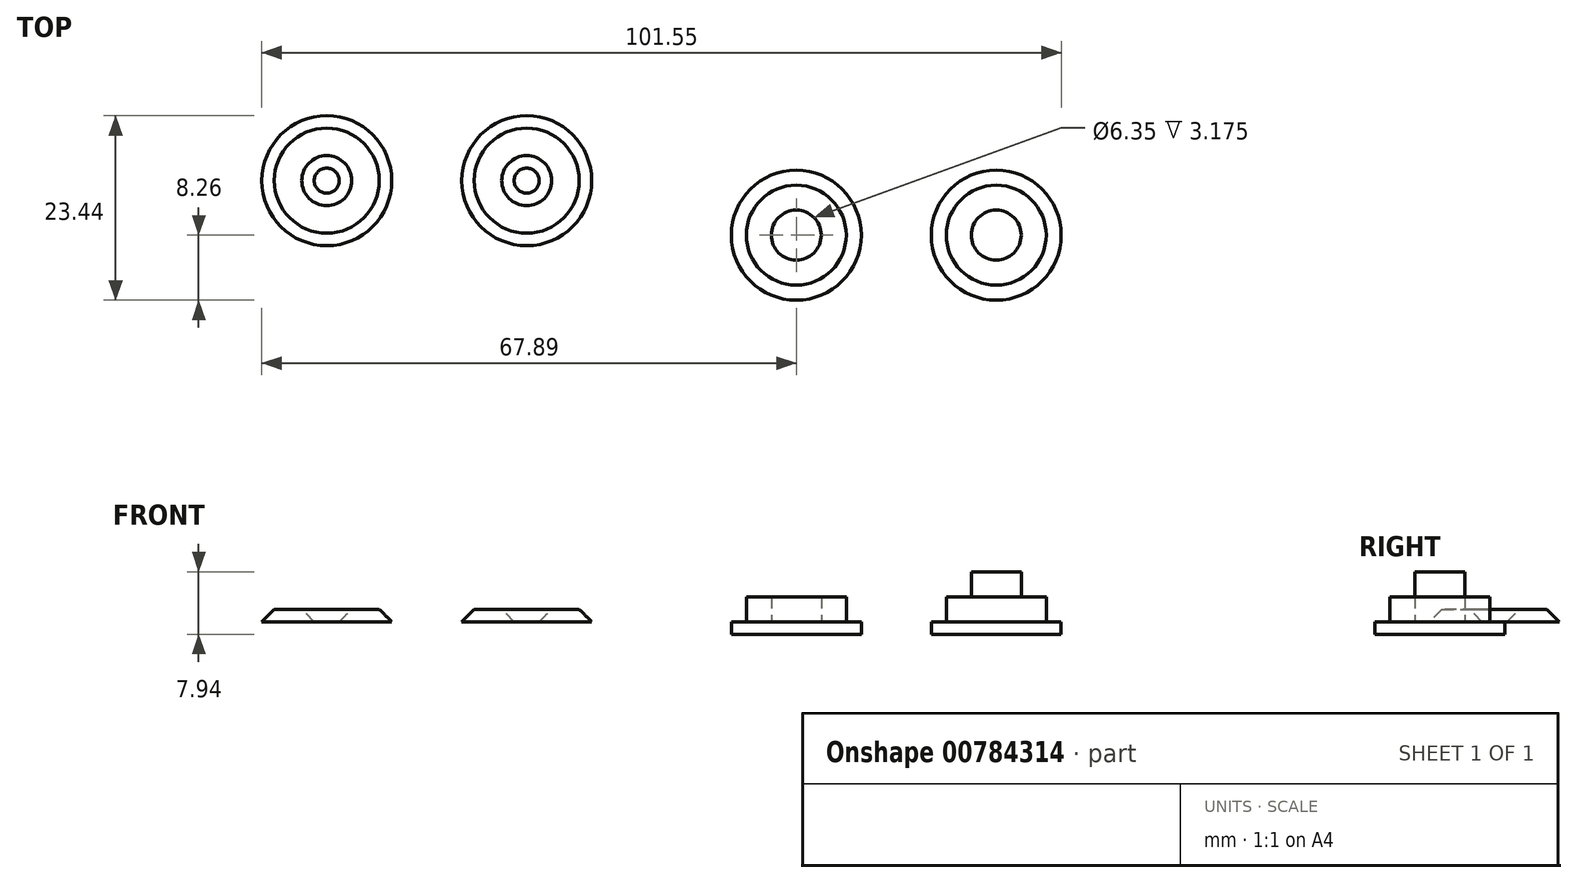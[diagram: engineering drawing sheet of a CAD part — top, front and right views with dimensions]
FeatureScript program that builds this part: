
annotation { "Feature Type Name" : "Feature", "Feature Type Description" : "" }
export const myFeature = defineFeature(function(context is Context, id is Id, definition is map)
    precondition{}
    {
        {
            var Q0;
            Q0=qCreatedBy(makeId("Top.planeOp"),FACE);
            var sketch = newSketch(context, id + "F0", { "sketchPlane" : qUnion([Q0])});
            skCircle(sketch, "E0", {"center": v(0, 0) * mm, "radius": 6.35 * mm});
            skCircle(sketch, "E1", {"center": v(0, 0) * mm, "radius": 3.18 * mm});
            skSolve(sketch);
        }
        {
            var Q0;
            Q0 = qSketchRegion(id + "F0", true);
            extrude(context, id + "F1", {"entities" : qUnion([Q0]), "depth" : 3.17 * mm, "offsetDistance" : 25.4 * mm});
        }
        {
            var Q0;
            Q0=makeQuery(id+"F1.opExtrude","CAP_FACE",FACE,{"disambiguationData":[OSD([sQuery(id+"F0.wireOp",EDGE,"E0"),sQuery(id+"F0.wireOp",EDGE,"E1")])],"isStart":true});
            var sketch = newSketch(context, id + "F2", { "sketchPlane" : qUnion([Q0])});
            skCircle(sketch, "E2", {"center": v(0, 0) * mm, "radius": 8.26 * mm});
            skSolve(sketch);
        }
        {
            var Q0;
            Q0 = qSketchRegion(id + "F2", true);
            extrude(context, id + "F3", {"entities" : qUnion([Q0]), "operationType" : NewBodyOperationType.ADD, "depth" : 3.17 * mm, "offsetDistance" : 25.4 * mm});
        }
        {
            var Q0;
            Q0=makeQuery(id+"F1.opExtrude","SWEPT_BODY",BODY,{"disambiguationData":[OSD([sQuery(id+"F0.wireOp",EDGE,"E0"),sQuery(id+"F0.wireOp",EDGE,"E1")])]});
            var Q1;
            Q1=qCreatedBy(makeId("Right.planeOp"),FACE);
            transform(context, id + "F4", {"entities" : qUnion([Q0]), "transformType" : TransformType.TRANSLATION_DISTANCE, "transformDirection" : qUnion([Q1]), "distance" : 25.4 * mm, "makeCopy" : true});
        }
        {
            var Q0;
            Q0=qCreatedBy(makeId("Top.planeOp"),FACE);
            var sketch = newSketch(context, id + "F5", { "sketchPlane" : qUnion([Q0])});
            skCircle(sketch, "E3", {"center": v(54.82, 6.15) * mm, "radius": 3.18 * mm});
            skSolve(sketch);
        }
        {
            var Q0;
            Q0 = qSketchRegion(id + "F5", true);
            extrude(context, id + "F6", {"entities" : qUnion([Q0]), "depth" : 6.35 * mm, "offsetDistance" : 25.4 * mm});
        }
        {
            var Q0;
            Q0=makeQuery(id+"F6.opExtrude","CAP_FACE",FACE,{"disambiguationData":[OSD([sQuery(id+"F5.wireOp",EDGE,"E3")])],"isStart":false});
            var sketch = newSketch(context, id + "F7", { "sketchPlane" : qUnion([Q0])});
            skLineSegment(sketch, "E4.bottom", {"start": v(54.82, 4.88) * mm, "end": v(58.63, 4.88) * mm});
            skLineSegment(sketch, "E4.top", {"start": v(54.82, 7.42) * mm, "end": v(58.63, 7.42) * mm});
            skLineSegment(sketch, "E4.left", {"start": v(54.82, 4.88) * mm, "end": v(54.82, 7.42) * mm});
            skLineSegment(sketch, "E4.right", {"start": v(58.63, 4.88) * mm, "end": v(58.63, 7.42) * mm});
            skLineSegment(sketch, "E5", {"start": v(54.82, 6.15) * mm, "end": v(54.82, 2.98) * mm});
            skLineSegment(sketch, "E6", {"start": v(54.82, 2.98) * mm, "end": v(54.82, 9.33) * mm});
            skSolve(sketch);
        }
        {
            var Q0;
            Q0 = qSketchRegion(id + "F7", true);
            extrude(context, id + "F8", {"entities" : qUnion([Q0]), "operationType" : NewBodyOperationType.ADD, "oppositeDirection" : true, "depth" : 3.17 * mm, "offsetDistance" : 25.4 * mm});
        }
        {
            var Q0;
            Q0=makeQuery(id+"F6.opExtrude","SWEPT_BODY",BODY,{"disambiguationData":[OSD([sQuery(id+"F5.wireOp",EDGE,"E3")])]});
            deleteBodies(context, id + "F9", {"entities" : qUnion([Q0])});
        }
        {
            var Q0;
            Q0=makeQuery(id+"F4.opPattern","COPY",FACE,{"derivedFrom":makeQuery(id+"F3.boolean.opBoolean","SPLIT",FACE,{"disambiguationData":[TD([makeQuery(id+"F1.opExtrude","SWEPT_FACE",FACE,{"disambiguationData":[OSD([sQuery(id+"F0.wireOp",EDGE,"E1")])]})])],"derivedFrom":makeQuery(id+"F3.opExtrude","CAP_FACE",FACE,{"disambiguationData":[OSD([sQuery(id+"F2.wireOp",EDGE,"E2")])],"isStart":true})}),"instanceName":"1"});
            extrude(context, id + "F10", {"entities" : qUnion([Q0]), "operationType" : NewBodyOperationType.ADD, "depth" : 6.35 * mm, "offsetDistance" : 25.4 * mm});
        }
        {
            var Q0;
            Q0=makeQuery(id+"F4.opPattern","COPY",FACE,{"derivedFrom":makeQuery(id+"F3.opExtrude","CAP_FACE",FACE,{"disambiguationData":[OSD([sQuery(id+"F2.wireOp",EDGE,"E2")])],"isStart":false}),"instanceName":"1"});
            extrude(context, id + "F11", {"entities" : qUnion([Q0]), "operationType" : NewBodyOperationType.REMOVE, "oppositeDirection" : true, "depth" : 1.59 * mm, "offsetDistance" : 25.4 * mm});
        }
        {
            var Q0;
            Q0=qCreatedBy(makeId("Top.planeOp"),FACE);
            var sketch = newSketch(context, id + "F12", { "sketchPlane" : qUnion([Q0])});
            skCircle(sketch, "E7", {"center": v(-34.24, 6.92) * mm, "radius": 8.26 * mm});
            skSolve(sketch);
        }
        {
            var Q0;
            Q0 = qSketchRegion(id + "F12", true);
            extrude(context, id + "F13", {"entities" : qUnion([Q0]), "depth" : 1.59 * mm, "offsetDistance" : 25.4 * mm, "hasDraft" : true, "draftAngle" : 45 * degree, "draftPullDirection" : true});
        }
        {
            var Q0;
            Q0=makeQuery(id+"F13.opExtrude","CAP_FACE",FACE,{"disambiguationData":[OSD([sQuery(id+"F12.wireOp",EDGE,"E7")])],"isStart":false});
            var sketch = newSketch(context, id + "F14", { "sketchPlane" : qUnion([Q0])});
            skCircle(sketch, "E8", {"center": v(-34.24, 6.92) * mm, "radius": 3.17 * mm});
            skSolve(sketch);
        }
        {
            var Q0;
            Q0=makeQuery(id+"F14.imprint","IMPRINT",FACE,{"disambiguationData":[TD([[makeQuery(id+"F14.imprint","IMPRINT",EDGE,{"derivedFrom":sQuery(id+"F14.wireOp",EDGE,"E8")}),1.0]])]});
            extrude(context, id + "F15", {"entities" : qUnion([Q0]), "operationType" : NewBodyOperationType.REMOVE, "oppositeDirection" : true, "depth" : 25.4 * mm, "offsetDistance" : 25.4 * mm, "hasDraft" : true, "draftAngle" : 45 * degree, "draftPullDirection" : true});
        }
        {
            var Q0;
            Q0=makeQuery(id+"F3.opExtrude","CAP_FACE",FACE,{"disambiguationData":[OSD([sQuery(id+"F2.wireOp",EDGE,"E2")])],"isStart":false});
            extrude(context, id + "F16", {"entities" : qUnion([Q0]), "operationType" : NewBodyOperationType.REMOVE, "oppositeDirection" : true, "depth" : 1.59 * mm, "offsetDistance" : 25.4 * mm});
        }
        {
            var Q0;
            Q0=makeQuery(id+"F13.opExtrude","SWEPT_BODY",BODY,{"disambiguationData":[OSD([sQuery(id+"F12.wireOp",EDGE,"E7")])]});
            var Q1;
            Q1=qCreatedBy(makeId("Right.planeOp"),FACE);
            transform(context, id + "F17", {"entities" : qUnion([Q0]), "transformType" : TransformType.TRANSLATION_DISTANCE, "transformDirection" : qUnion([Q1]), "distance" : 25.4 * mm, "oppositeDirection" : true, "makeCopy" : true});
        }
    });
